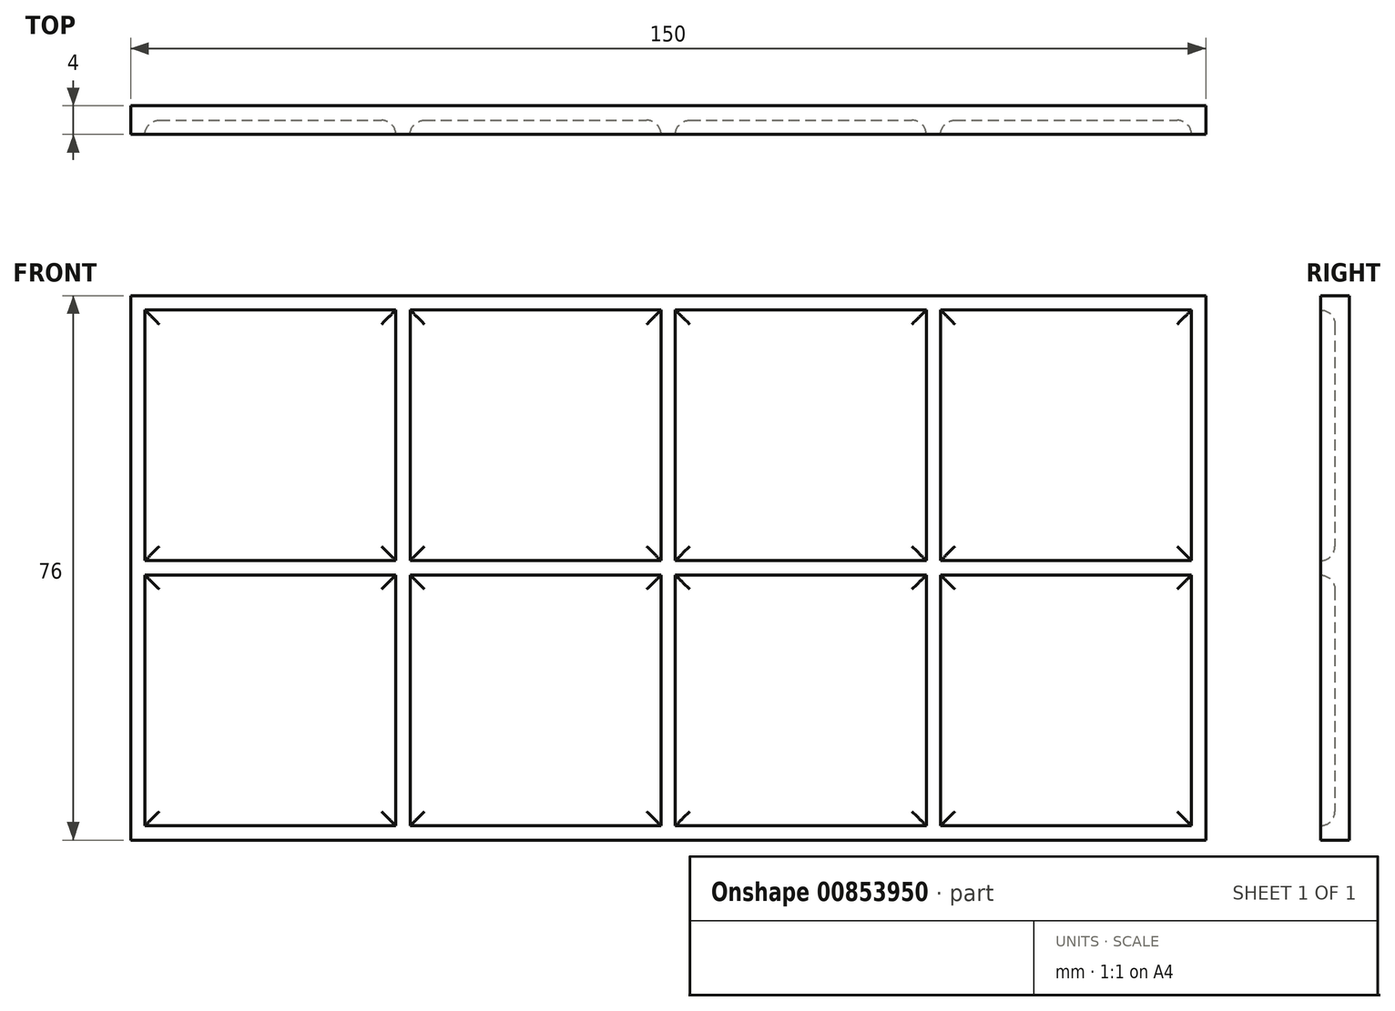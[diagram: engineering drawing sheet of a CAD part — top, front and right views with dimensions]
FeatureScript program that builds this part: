
annotation { "Feature Type Name" : "Feature", "Feature Type Description" : "" }
export const myFeature = defineFeature(function(context is Context, id is Id, definition is map)
    precondition{}
    {
        {
            var Q0;
            Q0=qCreatedBy(makeId("Front.planeOp"),FACE);
            var sketch = newSketch(context, id + "F0", { "sketchPlane" : qUnion([Q0])});
            skLineSegment(sketch, "E0.bottom", {"start": v(-75, 38) * mm, "end": v(75, 38) * mm});
            skLineSegment(sketch, "E0.top", {"start": v(-75, -38) * mm, "end": v(75, -38) * mm});
            skLineSegment(sketch, "E0.left", {"start": v(-75, 38) * mm, "end": v(-75, -38) * mm});
            skLineSegment(sketch, "E0.right", {"start": v(75, 38) * mm, "end": v(75, -38) * mm});
            skPoint(sketch, "E0.middle", {"position": v(0, 0) * mm});
            skLineSegment(sketch, "E1.bottom", {"start": v(1, 38) * mm, "end": v(-1, 38) * mm, "construction": true});
            skLineSegment(sketch, "E1.top", {"start": v(1, -38) * mm, "end": v(-1, -38) * mm, "construction": true});
            skLineSegment(sketch, "E1.left", {"start": v(1, 38) * mm, "end": v(1, -38) * mm, "construction": true});
            skLineSegment(sketch, "E1.right", {"start": v(-1, 38) * mm, "end": v(-1, -38) * mm, "construction": true});
            skLineSegment(sketch, "E2.bottom", {"start": v(-75, 1) * mm, "end": v(75, 1) * mm, "construction": true});
            skLineSegment(sketch, "E2.top", {"start": v(-75, -1) * mm, "end": v(75, -1) * mm, "construction": true});
            skLineSegment(sketch, "E2.left", {"start": v(-75, 1) * mm, "end": v(-75, -1) * mm, "construction": true});
            skLineSegment(sketch, "E2.right", {"start": v(75, 1) * mm, "end": v(75, -1) * mm, "construction": true});
            skLineSegment(sketch, "E3.bottom", {"start": v(-1, 1) * mm, "end": v(-36, 1) * mm});
            skLineSegment(sketch, "E3.top", {"start": v(-1, 36) * mm, "end": v(-36, 36) * mm});
            skLineSegment(sketch, "E3.left", {"start": v(-1, 1) * mm, "end": v(-1, 36) * mm});
            skLineSegment(sketch, "E3.right", {"start": v(-36, 1) * mm, "end": v(-36, 36) * mm});
            skLineSegment(sketch, "E4.bottom", {"start": v(-38, 1) * mm, "end": v(-73, 1) * mm});
            skLineSegment(sketch, "E4.top", {"start": v(-38, 36) * mm, "end": v(-73, 36) * mm});
            skLineSegment(sketch, "E4.left", {"start": v(-38, 1) * mm, "end": v(-38, 36) * mm});
            skLineSegment(sketch, "E4.right", {"start": v(-73, 1) * mm, "end": v(-73, 36) * mm});
            skLineSegment(sketch, "E5.bottom", {"start": v(73, 1) * mm, "end": v(38, 1) * mm});
            skLineSegment(sketch, "E5.top", {"start": v(73, 36) * mm, "end": v(38, 36) * mm});
            skLineSegment(sketch, "E5.left", {"start": v(73, 1) * mm, "end": v(73, 36) * mm});
            skLineSegment(sketch, "E5.right", {"start": v(38, 1) * mm, "end": v(38, 36) * mm});
            skLineSegment(sketch, "E6.bottom", {"start": v(36, 1) * mm, "end": v(1, 1) * mm});
            skLineSegment(sketch, "E6.top", {"start": v(36, 36) * mm, "end": v(1, 36) * mm});
            skLineSegment(sketch, "E6.left", {"start": v(36, 1) * mm, "end": v(36, 36) * mm});
            skLineSegment(sketch, "E6.right", {"start": v(1, 1) * mm, "end": v(1, 36) * mm});
            skLineSegment(sketch, "E7.bottom", {"start": v(-1, 1) * mm, "end": v(1, 1) * mm, "construction": true});
            skLineSegment(sketch, "E7.top", {"start": v(-1, -1) * mm, "end": v(1, -1) * mm, "construction": true});
            skLineSegment(sketch, "E7.left", {"start": v(-1, 1) * mm, "end": v(-1, -1) * mm, "construction": true});
            skLineSegment(sketch, "E7.right", {"start": v(1, 1) * mm, "end": v(1, -1) * mm, "construction": true});
            skLineSegment(sketch, "E8.bottom", {"start": v(-1, -36) * mm, "end": v(-36, -36) * mm});
            skLineSegment(sketch, "E8.top", {"start": v(-1, -1) * mm, "end": v(-36, -1) * mm});
            skLineSegment(sketch, "E8.left", {"start": v(-1, -36) * mm, "end": v(-1, -1) * mm});
            skLineSegment(sketch, "E8.right", {"start": v(-36, -36) * mm, "end": v(-36, -1) * mm});
            skLineSegment(sketch, "E9.bottom", {"start": v(-38, -36) * mm, "end": v(-73, -36) * mm});
            skLineSegment(sketch, "E9.top", {"start": v(-38, -1) * mm, "end": v(-73, -1) * mm});
            skLineSegment(sketch, "E9.left", {"start": v(-38, -36) * mm, "end": v(-38, -1) * mm});
            skLineSegment(sketch, "E9.right", {"start": v(-73, -36) * mm, "end": v(-73, -1) * mm});
            skLineSegment(sketch, "E10.bottom", {"start": v(73, -36) * mm, "end": v(38, -36) * mm});
            skLineSegment(sketch, "E10.top", {"start": v(73, -1) * mm, "end": v(38, -1) * mm});
            skLineSegment(sketch, "E10.left", {"start": v(73, -36) * mm, "end": v(73, -1) * mm});
            skLineSegment(sketch, "E10.right", {"start": v(38, -36) * mm, "end": v(38, -1) * mm});
            skLineSegment(sketch, "E11.bottom", {"start": v(36, -36) * mm, "end": v(1, -36) * mm});
            skLineSegment(sketch, "E11.top", {"start": v(36, -1) * mm, "end": v(1, -1) * mm});
            skLineSegment(sketch, "E11.left", {"start": v(36, -36) * mm, "end": v(36, -1) * mm});
            skLineSegment(sketch, "E11.right", {"start": v(1, -36) * mm, "end": v(1, -1) * mm});
            skSolve(sketch);
        }
        {
            var Q0;
            Q0=makeQuery(id+"F0.imprint","IMPRINT",FACE,{"disambiguationData":[TD([[makeQuery(id+"F0.imprint","IMPRINT",EDGE,{"derivedFrom":sQuery(id+"F0.wireOp",EDGE,"E0.bottom")}),-1.0]])]});
            var Q1;
            Q1=makeQuery(id+"F0.imprint","IMPRINT",FACE,{"disambiguationData":[TD([[makeQuery(id+"F0.imprint","IMPRINT",EDGE,{"derivedFrom":sQuery(id+"F0.wireOp",EDGE,"E9.bottom")}),-1.0]])]});
            var Q2;
            Q2=makeQuery(id+"F0.imprint","IMPRINT",FACE,{"disambiguationData":[TD([[makeQuery(id+"F0.imprint","IMPRINT",EDGE,{"derivedFrom":sQuery(id+"F0.wireOp",EDGE,"E4.bottom")}),-1.0]])]});
            var Q3;
            Q3=makeQuery(id+"F0.imprint","IMPRINT",FACE,{"disambiguationData":[TD([[makeQuery(id+"F0.imprint","IMPRINT",EDGE,{"derivedFrom":sQuery(id+"F0.wireOp",EDGE,"E3.bottom")}),-1.0]])]});
            var Q4;
            Q4=makeQuery(id+"F0.imprint","IMPRINT",FACE,{"disambiguationData":[TD([[makeQuery(id+"F0.imprint","IMPRINT",EDGE,{"derivedFrom":sQuery(id+"F0.wireOp",EDGE,"E6.bottom")}),-1.0]])]});
            var Q5;
            Q5=makeQuery(id+"F0.imprint","IMPRINT",FACE,{"disambiguationData":[TD([[makeQuery(id+"F0.imprint","IMPRINT",EDGE,{"derivedFrom":sQuery(id+"F0.wireOp",EDGE,"E10.bottom")}),-1.0]])]});
            var Q6;
            Q6=makeQuery(id+"F0.imprint","IMPRINT",FACE,{"disambiguationData":[TD([[makeQuery(id+"F0.imprint","IMPRINT",EDGE,{"derivedFrom":sQuery(id+"F0.wireOp",EDGE,"E5.bottom")}),-1.0]])]});
            var Q7;
            Q7=makeQuery(id+"F0.imprint","IMPRINT",FACE,{"disambiguationData":[TD([[makeQuery(id+"F0.imprint","IMPRINT",EDGE,{"derivedFrom":sQuery(id+"F0.wireOp",EDGE,"E11.bottom")}),-1.0]])]});
            var Q8;
            Q8=makeQuery(id+"F0.imprint","IMPRINT",FACE,{"disambiguationData":[TD([[makeQuery(id+"F0.imprint","IMPRINT",EDGE,{"derivedFrom":sQuery(id+"F0.wireOp",EDGE,"E8.bottom")}),-1.0]])]});
            extrude(context, id + "F1", {"entities" : qUnion([Q0, Q1, Q2, Q3, Q4, Q5, Q6, Q7, Q8]), "depth" : 2 * mm, "offsetDistance" : 25 * mm});
        }
        {
            var Q0;
            Q0 = qSketchRegion(id + "F0", true);
            var Q1;
            Q1=sQuery(id+"F0.wireOp",EDGE,"E9.left");
            var Q2;
            Q2=sQuery(id+"F0.wireOp",EDGE,"E8.right");
            extrude(context, id + "F2", {"entities" : qUnion([Q0]), "operationType" : NewBodyOperationType.ADD, "surfaceOperationType" : NewSurfaceOperationType.ADD, "surfaceEntities" : qUnion([Q1, Q2]), "depth" : 4 * mm, "offsetDistance" : 25 * mm});
        }
        {
            var Q0;
            Q0=makeQuery(id+"F2.boolean.opBoolean","INTERSECT",EDGE,{"derivedFrom":[makeQuery(id+"F1.opExtrude","CAP_FACE",FACE,{"disambiguationData":[OSD([sQuery(id+"F0.wireOp",EDGE,"E0.bottom"),sQuery(id+"F0.wireOp",EDGE,"E0.top"),sQuery(id+"F0.wireOp",EDGE,"E0.left"),sQuery(id+"F0.wireOp",EDGE,"E0.right")])],"isStart":false}),makeQuery(id+"F2.opExtrude","SWEPT_FACE",FACE,{"disambiguationData":[OSD([sQuery(id+"F0.wireOp",EDGE,"E9.right")])]})]});
            var Q1;
            Q1=makeQuery(id+"F2.boolean.opBoolean","INTERSECT",EDGE,{"derivedFrom":[makeQuery(id+"F1.opExtrude","CAP_FACE",FACE,{"disambiguationData":[OSD([sQuery(id+"F0.wireOp",EDGE,"E0.bottom"),sQuery(id+"F0.wireOp",EDGE,"E0.top"),sQuery(id+"F0.wireOp",EDGE,"E0.left"),sQuery(id+"F0.wireOp",EDGE,"E0.right")])],"isStart":false}),makeQuery(id+"F2.opExtrude","SWEPT_FACE",FACE,{"disambiguationData":[OSD([sQuery(id+"F0.wireOp",EDGE,"E9.top")])]})]});
            var Q2;
            Q2=makeQuery(id+"F2.boolean.opBoolean","INTERSECT",EDGE,{"derivedFrom":[makeQuery(id+"F1.opExtrude","CAP_FACE",FACE,{"disambiguationData":[OSD([sQuery(id+"F0.wireOp",EDGE,"E0.bottom"),sQuery(id+"F0.wireOp",EDGE,"E0.top"),sQuery(id+"F0.wireOp",EDGE,"E0.left"),sQuery(id+"F0.wireOp",EDGE,"E0.right")])],"isStart":false}),makeQuery(id+"F2.opExtrude","SWEPT_FACE",FACE,{"disambiguationData":[OSD([sQuery(id+"F0.wireOp",EDGE,"E4.top")])]})]});
            var Q3;
            Q3=makeQuery(id+"F2.boolean.opBoolean","INTERSECT",EDGE,{"derivedFrom":[makeQuery(id+"F1.opExtrude","CAP_FACE",FACE,{"disambiguationData":[OSD([sQuery(id+"F0.wireOp",EDGE,"E0.bottom"),sQuery(id+"F0.wireOp",EDGE,"E0.top"),sQuery(id+"F0.wireOp",EDGE,"E0.left"),sQuery(id+"F0.wireOp",EDGE,"E0.right")])],"isStart":false}),makeQuery(id+"F2.opExtrude","SWEPT_FACE",FACE,{"disambiguationData":[OSD([sQuery(id+"F0.wireOp",EDGE,"E3.right")])]})]});
            var Q4;
            Q4=makeQuery(id+"F2.boolean.opBoolean","INTERSECT",EDGE,{"derivedFrom":[makeQuery(id+"F1.opExtrude","CAP_FACE",FACE,{"disambiguationData":[OSD([sQuery(id+"F0.wireOp",EDGE,"E0.bottom"),sQuery(id+"F0.wireOp",EDGE,"E0.top"),sQuery(id+"F0.wireOp",EDGE,"E0.left"),sQuery(id+"F0.wireOp",EDGE,"E0.right")])],"isStart":false}),makeQuery(id+"F2.opExtrude","SWEPT_FACE",FACE,{"disambiguationData":[OSD([sQuery(id+"F0.wireOp",EDGE,"E3.top")])]})]});
            var Q5;
            Q5=makeQuery(id+"F2.boolean.opBoolean","INTERSECT",EDGE,{"derivedFrom":[makeQuery(id+"F1.opExtrude","CAP_FACE",FACE,{"disambiguationData":[OSD([sQuery(id+"F0.wireOp",EDGE,"E0.bottom"),sQuery(id+"F0.wireOp",EDGE,"E0.top"),sQuery(id+"F0.wireOp",EDGE,"E0.left"),sQuery(id+"F0.wireOp",EDGE,"E0.right")])],"isStart":false}),makeQuery(id+"F2.opExtrude","SWEPT_FACE",FACE,{"disambiguationData":[OSD([sQuery(id+"F0.wireOp",EDGE,"E4.right")])]})]});
            var Q6;
            Q6=makeQuery(id+"F2.boolean.opBoolean","INTERSECT",EDGE,{"derivedFrom":[makeQuery(id+"F1.opExtrude","CAP_FACE",FACE,{"disambiguationData":[OSD([sQuery(id+"F0.wireOp",EDGE,"E0.bottom"),sQuery(id+"F0.wireOp",EDGE,"E0.top"),sQuery(id+"F0.wireOp",EDGE,"E0.left"),sQuery(id+"F0.wireOp",EDGE,"E0.right")])],"isStart":false}),makeQuery(id+"F2.opExtrude","SWEPT_FACE",FACE,{"disambiguationData":[OSD([sQuery(id+"F0.wireOp",EDGE,"E6.right")])]})]});
            var Q7;
            Q7=makeQuery(id+"F2.boolean.opBoolean","INTERSECT",EDGE,{"derivedFrom":[makeQuery(id+"F1.opExtrude","CAP_FACE",FACE,{"disambiguationData":[OSD([sQuery(id+"F0.wireOp",EDGE,"E0.bottom"),sQuery(id+"F0.wireOp",EDGE,"E0.top"),sQuery(id+"F0.wireOp",EDGE,"E0.left"),sQuery(id+"F0.wireOp",EDGE,"E0.right")])],"isStart":false}),makeQuery(id+"F2.opExtrude","SWEPT_FACE",FACE,{"disambiguationData":[OSD([sQuery(id+"F0.wireOp",EDGE,"E6.top")])]})]});
            var Q8;
            Q8=makeQuery(id+"F2.boolean.opBoolean","INTERSECT",EDGE,{"derivedFrom":[makeQuery(id+"F1.opExtrude","CAP_FACE",FACE,{"disambiguationData":[OSD([sQuery(id+"F0.wireOp",EDGE,"E0.bottom"),sQuery(id+"F0.wireOp",EDGE,"E0.top"),sQuery(id+"F0.wireOp",EDGE,"E0.left"),sQuery(id+"F0.wireOp",EDGE,"E0.right")])],"isStart":false}),makeQuery(id+"F2.opExtrude","SWEPT_FACE",FACE,{"disambiguationData":[OSD([sQuery(id+"F0.wireOp",EDGE,"E5.right")])]})]});
            var Q9;
            Q9=makeQuery(id+"F2.boolean.opBoolean","INTERSECT",EDGE,{"derivedFrom":[makeQuery(id+"F1.opExtrude","CAP_FACE",FACE,{"disambiguationData":[OSD([sQuery(id+"F0.wireOp",EDGE,"E0.bottom"),sQuery(id+"F0.wireOp",EDGE,"E0.top"),sQuery(id+"F0.wireOp",EDGE,"E0.left"),sQuery(id+"F0.wireOp",EDGE,"E0.right")])],"isStart":false}),makeQuery(id+"F2.opExtrude","SWEPT_FACE",FACE,{"disambiguationData":[OSD([sQuery(id+"F0.wireOp",EDGE,"E5.top")])]})]});
            var Q10;
            Q10=makeQuery(id+"F2.boolean.opBoolean","INTERSECT",EDGE,{"derivedFrom":[makeQuery(id+"F1.opExtrude","CAP_FACE",FACE,{"disambiguationData":[OSD([sQuery(id+"F0.wireOp",EDGE,"E0.bottom"),sQuery(id+"F0.wireOp",EDGE,"E0.top"),sQuery(id+"F0.wireOp",EDGE,"E0.left"),sQuery(id+"F0.wireOp",EDGE,"E0.right")])],"isStart":false}),makeQuery(id+"F2.opExtrude","SWEPT_FACE",FACE,{"disambiguationData":[OSD([sQuery(id+"F0.wireOp",EDGE,"E10.top")])]})]});
            var Q11;
            Q11=makeQuery(id+"F2.boolean.opBoolean","INTERSECT",EDGE,{"derivedFrom":[makeQuery(id+"F1.opExtrude","CAP_FACE",FACE,{"disambiguationData":[OSD([sQuery(id+"F0.wireOp",EDGE,"E0.bottom"),sQuery(id+"F0.wireOp",EDGE,"E0.top"),sQuery(id+"F0.wireOp",EDGE,"E0.left"),sQuery(id+"F0.wireOp",EDGE,"E0.right")])],"isStart":false}),makeQuery(id+"F2.opExtrude","SWEPT_FACE",FACE,{"disambiguationData":[OSD([sQuery(id+"F0.wireOp",EDGE,"E10.right")])]})]});
            var Q12;
            Q12=makeQuery(id+"F2.boolean.opBoolean","INTERSECT",EDGE,{"derivedFrom":[makeQuery(id+"F1.opExtrude","CAP_FACE",FACE,{"disambiguationData":[OSD([sQuery(id+"F0.wireOp",EDGE,"E0.bottom"),sQuery(id+"F0.wireOp",EDGE,"E0.top"),sQuery(id+"F0.wireOp",EDGE,"E0.left"),sQuery(id+"F0.wireOp",EDGE,"E0.right")])],"isStart":false}),makeQuery(id+"F2.opExtrude","SWEPT_FACE",FACE,{"disambiguationData":[OSD([sQuery(id+"F0.wireOp",EDGE,"E11.top")])]})]});
            var Q13;
            Q13=makeQuery(id+"F2.boolean.opBoolean","INTERSECT",EDGE,{"derivedFrom":[makeQuery(id+"F1.opExtrude","CAP_FACE",FACE,{"disambiguationData":[OSD([sQuery(id+"F0.wireOp",EDGE,"E0.bottom"),sQuery(id+"F0.wireOp",EDGE,"E0.top"),sQuery(id+"F0.wireOp",EDGE,"E0.left"),sQuery(id+"F0.wireOp",EDGE,"E0.right")])],"isStart":false}),makeQuery(id+"F2.opExtrude","SWEPT_FACE",FACE,{"disambiguationData":[OSD([sQuery(id+"F0.wireOp",EDGE,"E11.right")])]})]});
            var Q14;
            Q14=makeQuery(id+"F2.boolean.opBoolean","INTERSECT",EDGE,{"derivedFrom":[makeQuery(id+"F1.opExtrude","CAP_FACE",FACE,{"disambiguationData":[OSD([sQuery(id+"F0.wireOp",EDGE,"E0.bottom"),sQuery(id+"F0.wireOp",EDGE,"E0.top"),sQuery(id+"F0.wireOp",EDGE,"E0.left"),sQuery(id+"F0.wireOp",EDGE,"E0.right")])],"isStart":false}),makeQuery(id+"F2.opExtrude","SWEPT_FACE",FACE,{"disambiguationData":[OSD([sQuery(id+"F0.wireOp",EDGE,"E8.top")])]})]});
            var Q15;
            Q15=makeQuery(id+"F2.boolean.opBoolean","INTERSECT",EDGE,{"derivedFrom":[makeQuery(id+"F1.opExtrude","CAP_FACE",FACE,{"disambiguationData":[OSD([sQuery(id+"F0.wireOp",EDGE,"E0.bottom"),sQuery(id+"F0.wireOp",EDGE,"E0.top"),sQuery(id+"F0.wireOp",EDGE,"E0.left"),sQuery(id+"F0.wireOp",EDGE,"E0.right")])],"isStart":false}),makeQuery(id+"F2.opExtrude","SWEPT_FACE",FACE,{"disambiguationData":[OSD([sQuery(id+"F0.wireOp",EDGE,"E8.right")])]})]});
            var Q16;
            Q16=makeQuery(id+"F2.boolean.opBoolean","INTERSECT",EDGE,{"derivedFrom":[makeQuery(id+"F1.opExtrude","CAP_FACE",FACE,{"disambiguationData":[OSD([sQuery(id+"F0.wireOp",EDGE,"E0.bottom"),sQuery(id+"F0.wireOp",EDGE,"E0.top"),sQuery(id+"F0.wireOp",EDGE,"E0.left"),sQuery(id+"F0.wireOp",EDGE,"E0.right")])],"isStart":false}),makeQuery(id+"F2.opExtrude","SWEPT_FACE",FACE,{"disambiguationData":[OSD([sQuery(id+"F0.wireOp",EDGE,"E10.left")])]})]});
            var Q17;
            Q17=makeQuery(id+"F2.boolean.opBoolean","INTERSECT",EDGE,{"derivedFrom":[makeQuery(id+"F1.opExtrude","CAP_FACE",FACE,{"disambiguationData":[OSD([sQuery(id+"F0.wireOp",EDGE,"E0.bottom"),sQuery(id+"F0.wireOp",EDGE,"E0.top"),sQuery(id+"F0.wireOp",EDGE,"E0.left"),sQuery(id+"F0.wireOp",EDGE,"E0.right")])],"isStart":false}),makeQuery(id+"F2.opExtrude","SWEPT_FACE",FACE,{"disambiguationData":[OSD([sQuery(id+"F0.wireOp",EDGE,"E10.bottom")])]})]});
            var Q18;
            Q18=makeQuery(id+"F2.boolean.opBoolean","INTERSECT",EDGE,{"derivedFrom":[makeQuery(id+"F1.opExtrude","CAP_FACE",FACE,{"disambiguationData":[OSD([sQuery(id+"F0.wireOp",EDGE,"E0.bottom"),sQuery(id+"F0.wireOp",EDGE,"E0.top"),sQuery(id+"F0.wireOp",EDGE,"E0.left"),sQuery(id+"F0.wireOp",EDGE,"E0.right")])],"isStart":false}),makeQuery(id+"F2.opExtrude","SWEPT_FACE",FACE,{"disambiguationData":[OSD([sQuery(id+"F0.wireOp",EDGE,"E11.bottom")])]})]});
            var Q19;
            Q19=makeQuery(id+"F2.boolean.opBoolean","INTERSECT",EDGE,{"derivedFrom":[makeQuery(id+"F1.opExtrude","CAP_FACE",FACE,{"disambiguationData":[OSD([sQuery(id+"F0.wireOp",EDGE,"E0.bottom"),sQuery(id+"F0.wireOp",EDGE,"E0.top"),sQuery(id+"F0.wireOp",EDGE,"E0.left"),sQuery(id+"F0.wireOp",EDGE,"E0.right")])],"isStart":false}),makeQuery(id+"F2.opExtrude","SWEPT_FACE",FACE,{"disambiguationData":[OSD([sQuery(id+"F0.wireOp",EDGE,"E8.bottom")])]})]});
            var Q20;
            Q20=makeQuery(id+"F2.boolean.opBoolean","INTERSECT",EDGE,{"derivedFrom":[makeQuery(id+"F1.opExtrude","CAP_FACE",FACE,{"disambiguationData":[OSD([sQuery(id+"F0.wireOp",EDGE,"E0.bottom"),sQuery(id+"F0.wireOp",EDGE,"E0.top"),sQuery(id+"F0.wireOp",EDGE,"E0.left"),sQuery(id+"F0.wireOp",EDGE,"E0.right")])],"isStart":false}),makeQuery(id+"F2.opExtrude","SWEPT_FACE",FACE,{"disambiguationData":[OSD([sQuery(id+"F0.wireOp",EDGE,"E9.bottom")])]})]});
            var Q21;
            Q21=makeQuery(id+"F2.boolean.opBoolean","INTERSECT",EDGE,{"derivedFrom":[makeQuery(id+"F1.opExtrude","CAP_FACE",FACE,{"disambiguationData":[OSD([sQuery(id+"F0.wireOp",EDGE,"E0.bottom"),sQuery(id+"F0.wireOp",EDGE,"E0.top"),sQuery(id+"F0.wireOp",EDGE,"E0.left"),sQuery(id+"F0.wireOp",EDGE,"E0.right")])],"isStart":false}),makeQuery(id+"F2.opExtrude","SWEPT_FACE",FACE,{"disambiguationData":[OSD([sQuery(id+"F0.wireOp",EDGE,"E9.left")])]})]});
            var Q22;
            Q22=makeQuery(id+"F2.boolean.opBoolean","INTERSECT",EDGE,{"derivedFrom":[makeQuery(id+"F1.opExtrude","CAP_FACE",FACE,{"disambiguationData":[OSD([sQuery(id+"F0.wireOp",EDGE,"E0.bottom"),sQuery(id+"F0.wireOp",EDGE,"E0.top"),sQuery(id+"F0.wireOp",EDGE,"E0.left"),sQuery(id+"F0.wireOp",EDGE,"E0.right")])],"isStart":false}),makeQuery(id+"F2.opExtrude","SWEPT_FACE",FACE,{"disambiguationData":[OSD([sQuery(id+"F0.wireOp",EDGE,"E8.left")])]})]});
            var Q23;
            Q23=makeQuery(id+"F2.boolean.opBoolean","INTERSECT",EDGE,{"derivedFrom":[makeQuery(id+"F1.opExtrude","CAP_FACE",FACE,{"disambiguationData":[OSD([sQuery(id+"F0.wireOp",EDGE,"E0.bottom"),sQuery(id+"F0.wireOp",EDGE,"E0.top"),sQuery(id+"F0.wireOp",EDGE,"E0.left"),sQuery(id+"F0.wireOp",EDGE,"E0.right")])],"isStart":false}),makeQuery(id+"F2.opExtrude","SWEPT_FACE",FACE,{"disambiguationData":[OSD([sQuery(id+"F0.wireOp",EDGE,"E11.left")])]})]});
            var Q24;
            Q24=makeQuery(id+"F2.boolean.opBoolean","INTERSECT",EDGE,{"derivedFrom":[makeQuery(id+"F1.opExtrude","CAP_FACE",FACE,{"disambiguationData":[OSD([sQuery(id+"F0.wireOp",EDGE,"E0.bottom"),sQuery(id+"F0.wireOp",EDGE,"E0.top"),sQuery(id+"F0.wireOp",EDGE,"E0.left"),sQuery(id+"F0.wireOp",EDGE,"E0.right")])],"isStart":false}),makeQuery(id+"F2.opExtrude","SWEPT_FACE",FACE,{"disambiguationData":[OSD([sQuery(id+"F0.wireOp",EDGE,"E5.bottom")])]})]});
            var Q25;
            Q25=makeQuery(id+"F2.boolean.opBoolean","INTERSECT",EDGE,{"derivedFrom":[makeQuery(id+"F1.opExtrude","CAP_FACE",FACE,{"disambiguationData":[OSD([sQuery(id+"F0.wireOp",EDGE,"E0.bottom"),sQuery(id+"F0.wireOp",EDGE,"E0.top"),sQuery(id+"F0.wireOp",EDGE,"E0.left"),sQuery(id+"F0.wireOp",EDGE,"E0.right")])],"isStart":false}),makeQuery(id+"F2.opExtrude","SWEPT_FACE",FACE,{"disambiguationData":[OSD([sQuery(id+"F0.wireOp",EDGE,"E5.left")])]})]});
            var Q26;
            Q26=makeQuery(id+"F2.boolean.opBoolean","INTERSECT",EDGE,{"derivedFrom":[makeQuery(id+"F1.opExtrude","CAP_FACE",FACE,{"disambiguationData":[OSD([sQuery(id+"F0.wireOp",EDGE,"E0.bottom"),sQuery(id+"F0.wireOp",EDGE,"E0.top"),sQuery(id+"F0.wireOp",EDGE,"E0.left"),sQuery(id+"F0.wireOp",EDGE,"E0.right")])],"isStart":false}),makeQuery(id+"F2.opExtrude","SWEPT_FACE",FACE,{"disambiguationData":[OSD([sQuery(id+"F0.wireOp",EDGE,"E6.bottom")])]})]});
            var Q27;
            Q27=makeQuery(id+"F2.boolean.opBoolean","INTERSECT",EDGE,{"derivedFrom":[makeQuery(id+"F1.opExtrude","CAP_FACE",FACE,{"disambiguationData":[OSD([sQuery(id+"F0.wireOp",EDGE,"E0.bottom"),sQuery(id+"F0.wireOp",EDGE,"E0.top"),sQuery(id+"F0.wireOp",EDGE,"E0.left"),sQuery(id+"F0.wireOp",EDGE,"E0.right")])],"isStart":false}),makeQuery(id+"F2.opExtrude","SWEPT_FACE",FACE,{"disambiguationData":[OSD([sQuery(id+"F0.wireOp",EDGE,"E6.left")])]})]});
            var Q28;
            Q28=makeQuery(id+"F2.boolean.opBoolean","INTERSECT",EDGE,{"derivedFrom":[makeQuery(id+"F1.opExtrude","CAP_FACE",FACE,{"disambiguationData":[OSD([sQuery(id+"F0.wireOp",EDGE,"E0.bottom"),sQuery(id+"F0.wireOp",EDGE,"E0.top"),sQuery(id+"F0.wireOp",EDGE,"E0.left"),sQuery(id+"F0.wireOp",EDGE,"E0.right")])],"isStart":false}),makeQuery(id+"F2.opExtrude","SWEPT_FACE",FACE,{"disambiguationData":[OSD([sQuery(id+"F0.wireOp",EDGE,"E3.bottom")])]})]});
            var Q29;
            Q29=makeQuery(id+"F2.boolean.opBoolean","INTERSECT",EDGE,{"derivedFrom":[makeQuery(id+"F1.opExtrude","CAP_FACE",FACE,{"disambiguationData":[OSD([sQuery(id+"F0.wireOp",EDGE,"E0.bottom"),sQuery(id+"F0.wireOp",EDGE,"E0.top"),sQuery(id+"F0.wireOp",EDGE,"E0.left"),sQuery(id+"F0.wireOp",EDGE,"E0.right")])],"isStart":false}),makeQuery(id+"F2.opExtrude","SWEPT_FACE",FACE,{"disambiguationData":[OSD([sQuery(id+"F0.wireOp",EDGE,"E3.left")])]})]});
            var Q30;
            Q30=makeQuery(id+"F2.boolean.opBoolean","INTERSECT",EDGE,{"derivedFrom":[makeQuery(id+"F1.opExtrude","CAP_FACE",FACE,{"disambiguationData":[OSD([sQuery(id+"F0.wireOp",EDGE,"E0.bottom"),sQuery(id+"F0.wireOp",EDGE,"E0.top"),sQuery(id+"F0.wireOp",EDGE,"E0.left"),sQuery(id+"F0.wireOp",EDGE,"E0.right")])],"isStart":false}),makeQuery(id+"F2.opExtrude","SWEPT_FACE",FACE,{"disambiguationData":[OSD([sQuery(id+"F0.wireOp",EDGE,"E4.bottom")])]})]});
            var Q31;
            Q31=makeQuery(id+"F2.boolean.opBoolean","INTERSECT",EDGE,{"derivedFrom":[makeQuery(id+"F1.opExtrude","CAP_FACE",FACE,{"disambiguationData":[OSD([sQuery(id+"F0.wireOp",EDGE,"E0.bottom"),sQuery(id+"F0.wireOp",EDGE,"E0.top"),sQuery(id+"F0.wireOp",EDGE,"E0.left"),sQuery(id+"F0.wireOp",EDGE,"E0.right")])],"isStart":false}),makeQuery(id+"F2.opExtrude","SWEPT_FACE",FACE,{"disambiguationData":[OSD([sQuery(id+"F0.wireOp",EDGE,"E4.left")])]})]});
            fillet(context, id + "F3", {"entities" : qUnion([Q0, Q1, Q2, Q3, Q4, Q5, Q6, Q7, Q8, Q9, Q10, Q11, Q12, Q13, Q14, Q15, Q16, Q17, Q18, Q19, Q20, Q21, Q22, Q23, Q24, Q25, Q26, Q27, Q28, Q29, Q30, Q31]), "radius" : 2 * mm, "allowEdgeOverflow" : false});
        }
    });
